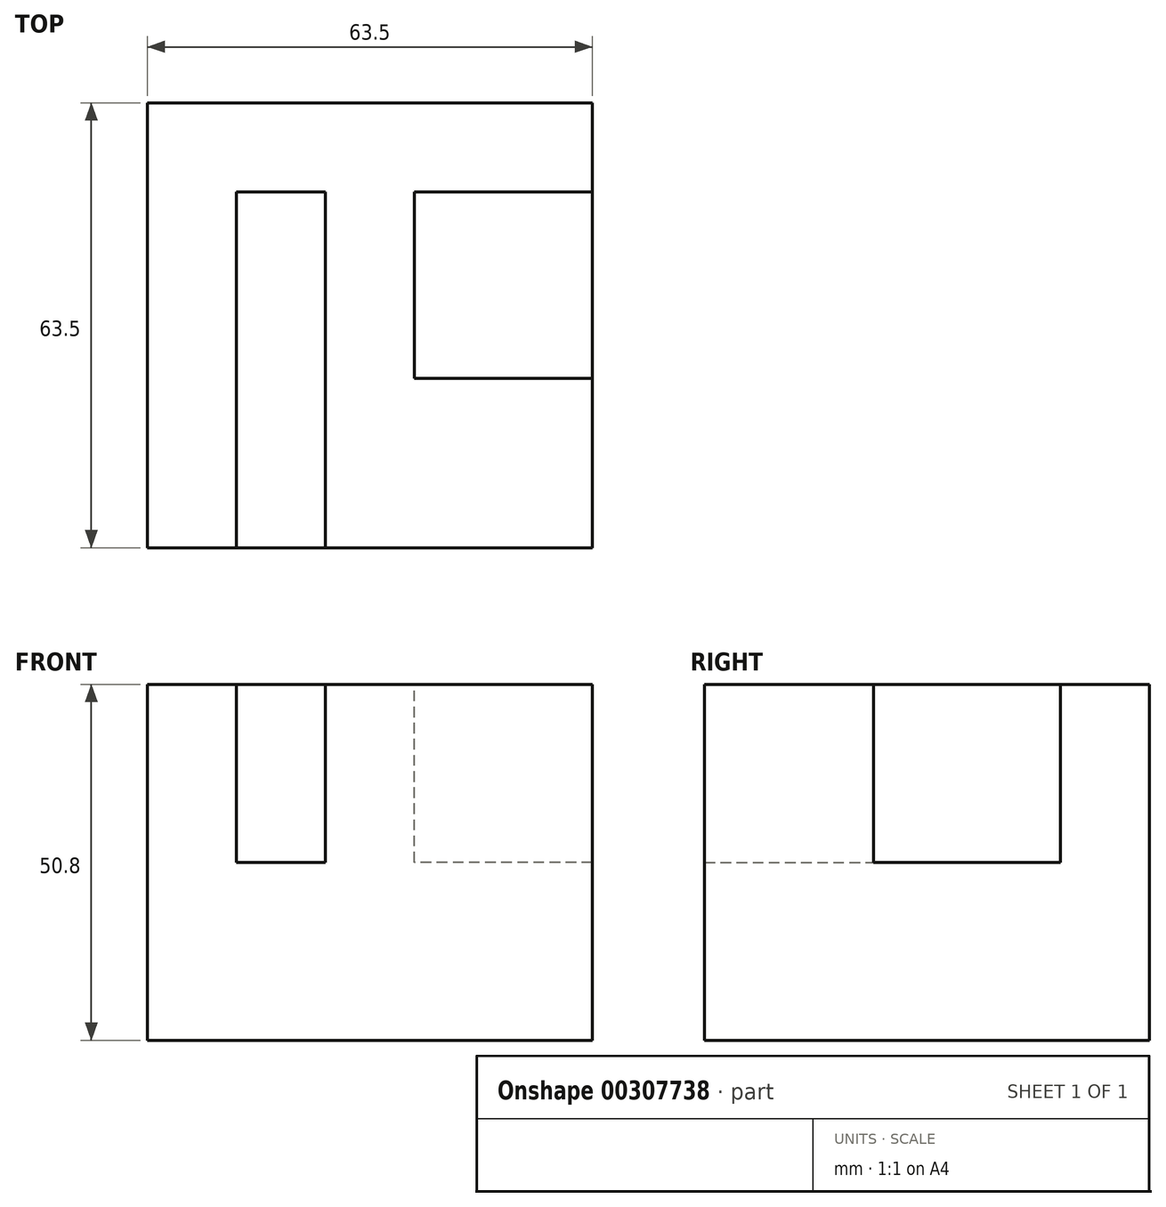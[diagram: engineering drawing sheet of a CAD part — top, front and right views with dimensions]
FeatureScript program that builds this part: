
annotation { "Feature Type Name" : "Feature", "Feature Type Description" : "" }
export const myFeature = defineFeature(function(context is Context, id is Id, definition is map)
    precondition{}
    {
        {
            var Q0;
            Q0=qCreatedBy(makeId("Top.planeOp"),FACE);
            var sketch = newSketch(context, id + "F0", { "sketchPlane" : qUnion([Q0])});
            skLineSegment(sketch, "E0", {"start": v(-41.5, -45.67) * mm, "end": v(22, -45.67) * mm});
            skLineSegment(sketch, "E1", {"start": v(22, -45.67) * mm, "end": v(22, 17.83) * mm});
            skLineSegment(sketch, "E2", {"start": v(22, 17.83) * mm, "end": v(-41.5, 17.83) * mm});
            skLineSegment(sketch, "E3", {"start": v(-41.5, 17.83) * mm, "end": v(-41.5, -45.67) * mm});
            skSolve(sketch);
        }
        {
            var Q0;
            Q0=makeQuery(id+"F0.imprint","IMPRINT",FACE,{"disambiguationData":[TD([[makeQuery(id+"F0.imprint","IMPRINT",EDGE,{"derivedFrom":sQuery(id+"F0.wireOp",EDGE,"E0")}),1.0]])]});
            extrude(context, id + "F1", {"entities" : qUnion([Q0]), "depth" : 50.8 * mm});
        }
        {
            var Q0;
            Q0=makeQuery(id+"F1.opExtrude","CAP_FACE",FACE,{"disambiguationData":[OSD([sQuery(id+"F0.wireOp",EDGE,"E0"),sQuery(id+"F0.wireOp",EDGE,"E1"),sQuery(id+"F0.wireOp",EDGE,"E2"),sQuery(id+"F0.wireOp",EDGE,"E3")])],"isStart":false});
            var sketch = newSketch(context, id + "F2", { "sketchPlane" : qUnion([Q0])});
            skLineSegment(sketch, "E4", {"start": v(-28.8, -45.67) * mm, "end": v(-28.8, 5.13) * mm});
            skLineSegment(sketch, "E5", {"start": v(-28.8, 5.13) * mm, "end": v(-16.1, 5.13) * mm});
            skLineSegment(sketch, "E6", {"start": v(-16.1, 5.13) * mm, "end": v(-16.1, -45.67) * mm});
            skLineSegment(sketch, "E7", {"start": v(22, 17.83) * mm, "end": v(22, 5.1) * mm});
            skLineSegment(sketch, "E8", {"start": v(22, 5.1) * mm, "end": v(-3.4, 5.1) * mm});
            skLineSegment(sketch, "E9", {"start": v(-3.4, 5.1) * mm, "end": v(-3.4, -21.51) * mm});
            skLineSegment(sketch, "E10", {"start": v(-3.4, -21.51) * mm, "end": v(22, -21.51) * mm});
            skLineSegment(sketch, "E11", {"start": v(22, -21.51) * mm, "end": v(22, 5.1) * mm});
            skSolve(sketch);
        }
        {
            var Q0;
            Q0=makeQuery(id+"F2.imprint","IMPRINT",FACE,{"disambiguationData":[TD([[makeQuery(id+"F2.imprint","IMPRINT",EDGE,{"derivedFrom":sQuery(id+"F2.wireOp",EDGE,"E8")}),1.0]])]});
            var Q1;
            {var subQ0=sQuery(id+"F2.wireOp",EDGE,"E4");Q1=makeQuery(id+"F2.imprint","IMPRINT",FACE,{"disambiguationData":[TD([[makeQuery(id+"F2.imprint","IMPRINT",EDGE,{"derivedFrom":subQ0}),-1.0]])]});}
            extrude(context, id + "F3", {"entities" : qUnion([Q0, Q1]), "operationType" : NewBodyOperationType.REMOVE, "oppositeDirection" : true, "depth" : 25.4 * mm});
        }
    });
